# Revit family: POOL LINEAL 18W ASIMETRICA_U2418AW.1
name_source: partatom
category: Luminarias
units: mm (PartAtom-declared; Revit-internal decimal feet)

## family parameters
Compartido = No
Corte con vacíos al cargar = No
Cota de conector redondo = Diámetro de uso
Origen de luz = Sí
Punto de cálculo de habitación = No
Se basa en plano de trabajo = Sí
Siempre vertical = No
Tipo de pieza = Normal

## types (1)
- SUB_U2418AW.1
    Archivo de red fotométrica = U2418SW.13000K.IES
    Cambio de temperatura de color de luz atenuada = <Ninguno>
    Comentarios de vataje = 24
    Descripción = LUMINARIA SUB ACUATICA TIPO LINEAL OPTICA ASIMETRICA, ACABADO EN ACERO INOXIDABLE, SELLO EN SILICON Y CUPERO MOLDEADO EN CROMO MIDIENDO 355MM DE LARGO POR 90MM CONSIDERANDO EL HOUSING, 6 LED TIPO NICHIA CON UN CONSUMO TOTAL DE 22.8W, 1102 LUMENES,  CON UNA TEMPERATURA EN BLANCO CALIDO DE 3000K, IP 68, IRC 80, IK 10, SUMERGIBLE MAXIMO 2M, CABLE H05RN DE 3M, UNICA APERTURA ASIMETRICA DE 45X35 GRADOS, ALIMENTADA A 24V. REQUIERE ACCESORIOS.
    Elevación por defecto = 0 mm  [stored 0 ft]
    Fabricante = BRILLANT
    Filtro de color = 16777215
    Lámpara = Nichia
    Modelo = U2418AW.1
    Watt per fixture = 22.8
    Ángulo de inclinación = 60.00°

note: [stored X ft] marks values corroborated as IEEE doubles in the binary element streams (Revit-internal decimal feet)

## geometry (parser evidence)
native form markers: Blend x2
no freeform markers — native parametric forms only
